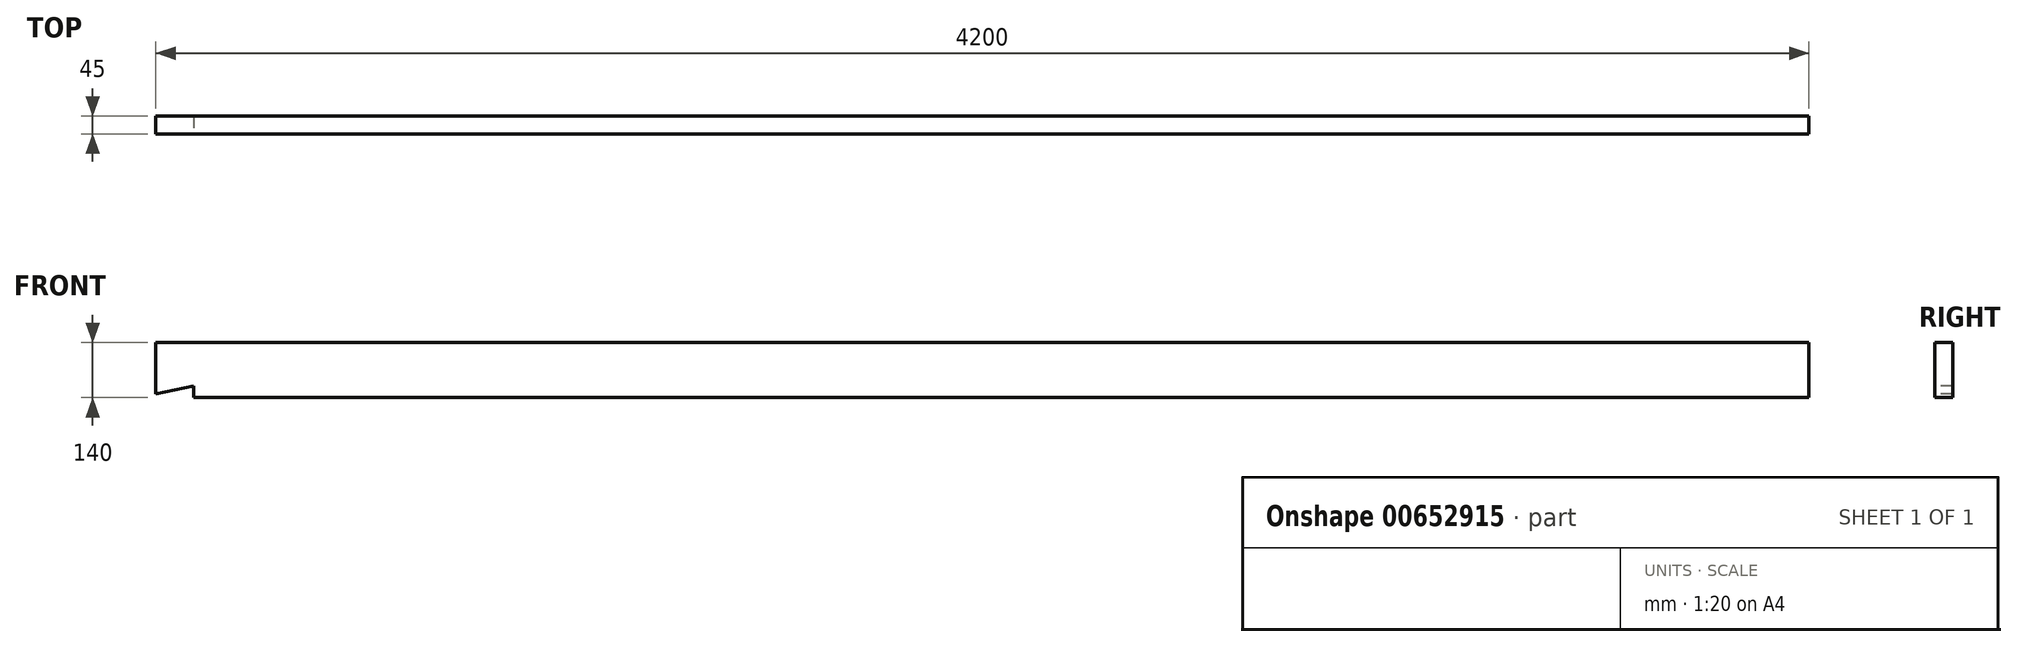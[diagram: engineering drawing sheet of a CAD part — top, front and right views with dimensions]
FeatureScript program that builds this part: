
annotation { "Feature Type Name" : "Feature", "Feature Type Description" : "" }
export const myFeature = defineFeature(function(context is Context, id is Id, definition is map)
    precondition{}
    {
        {
            var Q0;
            Q0=qCreatedBy(makeId("Right.planeOp"),FACE);
            var sketch = newSketch(context, id + "F0", { "sketchPlane" : qUnion([Q0])});
            skLineSegment(sketch, "E0.bottom", {"start": v(22.5, -70) * mm, "end": v(-22.5, -70) * mm});
            skLineSegment(sketch, "E0.top", {"start": v(22.5, 70) * mm, "end": v(-22.5, 70) * mm});
            skLineSegment(sketch, "E0.left", {"start": v(22.5, -70) * mm, "end": v(22.5, 70) * mm});
            skLineSegment(sketch, "E0.right", {"start": v(-22.5, -70) * mm, "end": v(-22.5, 70) * mm});
            skPoint(sketch, "E0.middle", {"position": v(0, 0) * mm});
            skSolve(sketch);
        }
        {
            var Q0;
            Q0 = qSketchRegion(id + "F0", true);
            extrude(context, id + "F1", {"entities" : qUnion([Q0]), "endBound" : BoundingType.SYMMETRIC, "depth" : 4200 * mm, "offsetDistance" : 25 * mm});
        }
        {
            var Q0;
            Q0=makeQuery(id+"F1.opExtrude","SWEPT_FACE",FACE,{"disambiguationData":[OSD([sQuery(id+"F0.wireOp",EDGE,"E0.right")])]});
            var sketch = newSketch(context, id + "F2", { "sketchPlane" : qUnion([Q0])});
            skLineSegment(sketch, "E1", {"start": v(-2100, -60) * mm, "end": v(-2003, -40) * mm});
            skLineSegment(sketch, "E2", {"start": v(-2003, -40) * mm, "end": v(-2003, -70) * mm});
            skLineSegment(sketch, "E3", {"start": v(-2003, -70) * mm, "end": v(-2100, -70) * mm});
            skLineSegment(sketch, "E4", {"start": v(-2100, -70) * mm, "end": v(-2100, -60) * mm});
            skSolve(sketch);
        }
        {
            var Q0;
            Q0 = qSketchRegion(id + "F2", true);
            extrude(context, id + "F3", {"entities" : qUnion([Q0]), "operationType" : NewBodyOperationType.REMOVE, "endBound" : BoundingType.UP_TO_NEXT, "oppositeDirection" : true, "depth" : 25 * mm, "offsetDistance" : 25 * mm});
        }
    });
